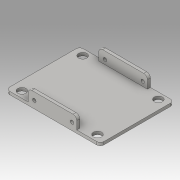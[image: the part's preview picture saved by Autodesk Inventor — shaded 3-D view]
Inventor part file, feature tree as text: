
AUTODESK INVENTOR PART (.ipt)
format: ipt  version: 2016 (Build 200138000, 138)  size: 205,312 bytes
history: native  units: in
note: dims shown in document units (in); Inventor stores cm internally (conversion verified against a paired STEP export)
features: sketch x9, extrude x6, hole x2, fillet x1
ambient origin geometry x8: Origin, YZ Plane, XZ Plane, XY Plane, X Axis, Y Axis, Z Axis, Center Point
bodies: Solid1 (feature_tree)
feature tree (18):
  extrude  "Extrusion1"  Depth=0.5in
  extrude  "Extrusion2"  Depth=0.1in
  extrude  "Extrusion3"  Depth=0.1in TaperAngle=0.0deg
  hole  "Hole1"  [1 undecoded]
  hole  "Hole2"  [1 undecoded]
  sketch  "Sketch6"  dims[d12=0.118in d13=0.75in d14=0.375in d15=0.25in d16=0.5635in d17=1.0in d18=0.8108in d19=4.0in]
  extrude  "Extrusion4"  Depth=0.713in
  extrude  "Extrusion5"  Depth=0.218in
  extrude  "Extrusion6"  Depth=0.125in
  fillet  "Fillet1"  Radius=0.218in
  sketch  "Sketch1"  dims[d0=4.0in d1=0.5in]
  sketch  "Sketch2"  dims[d2=0.1in d3=0.0in d4=0.1in]
  sketch  "Sketch3"  dims[d5=2.3in d6=0.0in d7=0.1in d8=0.0in]
  sketch  "Sketch4"  dims[d9=1.28in d10=0.25in]
  sketch  "Sketch5"  dims[d11=0.25in]
  sketch  "Sketch8"  dims[d20=1.36in d21=0.713in]
  sketch  "Sketch9"  dims[d22=0.218in d23=0.218in]
  sketch  "Sketch10"  dims[d24=0.72in d25=0.713in d26=0.218in d27=0.218in d28=0.72in d29=0.28in d30=0.75in d31=0.375in d32=0.25in d33=0.5635in d34=1.0in d35=0.8108in d36=0.581in d37=0.588in d38=0.0in d39=0.1in d40=1.0in d41=0.0in d42=0.4in d43=0.4in d44=1.0in d45=0.0in d46=0.1in d47=0.8in d48=1.0in d49=0.0in d50=0.125in d51=1.15in]
note: 2 required parameter values undecoded (feature->parameter linkage not recoverable at this tier; creation-order binding heuristic only, values carry confidence <= 0.55)
